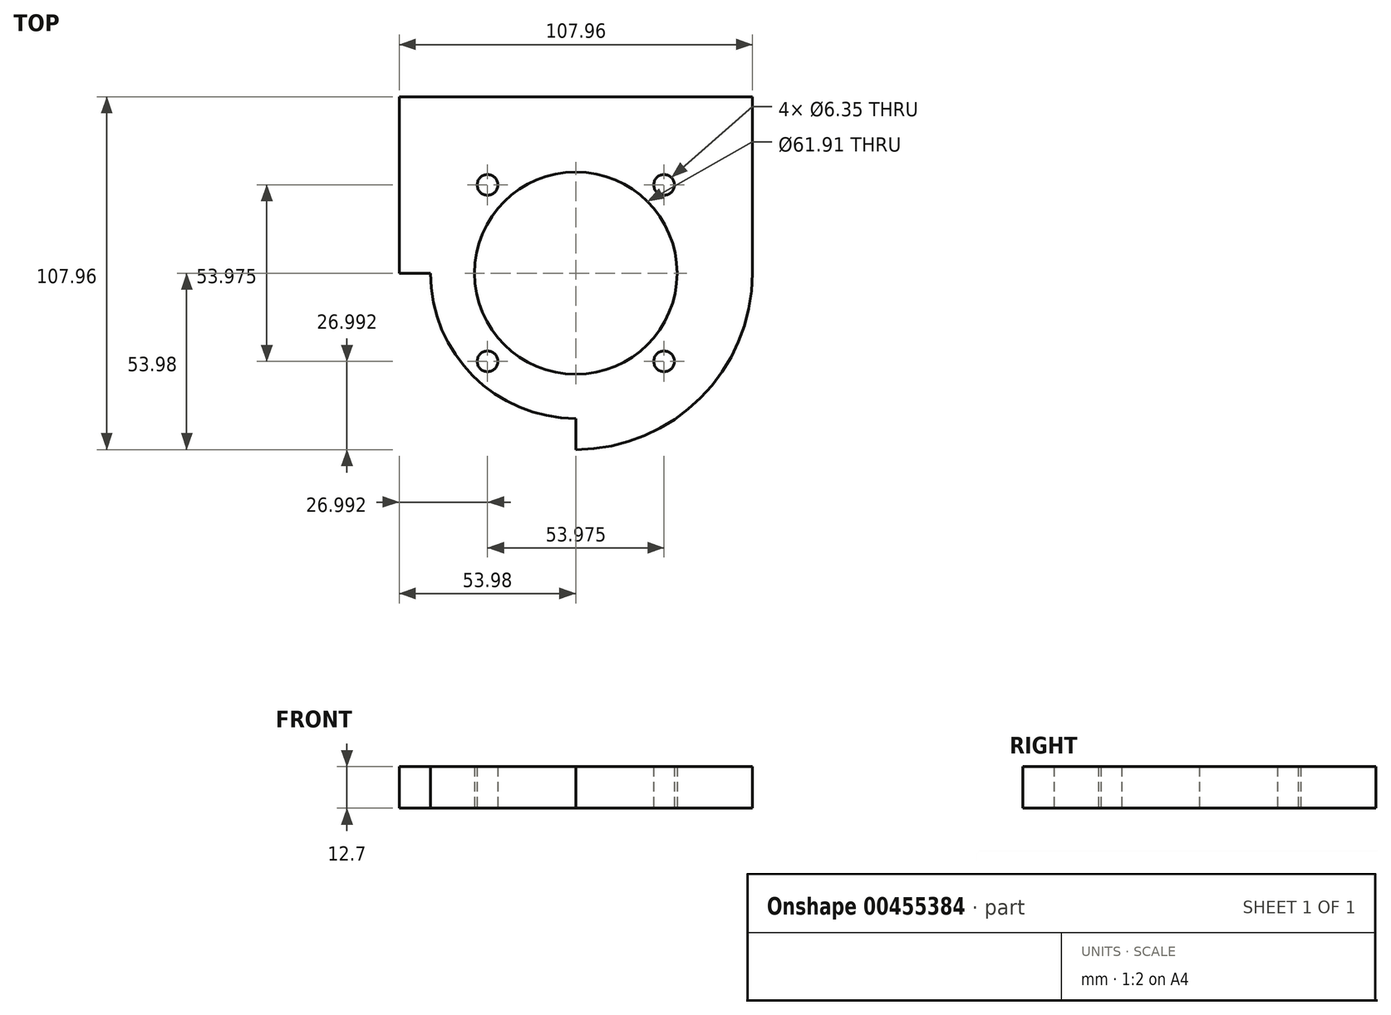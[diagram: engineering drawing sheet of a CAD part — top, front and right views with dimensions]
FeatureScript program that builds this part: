
annotation { "Feature Type Name" : "Feature", "Feature Type Description" : "" }
export const myFeature = defineFeature(function(context is Context, id is Id, definition is map)
    precondition{}
    {
        {
            var Q0;
            Q0=qCreatedBy(makeId("Top.planeOp"),FACE);
            var sketch = newSketch(context, id + "F0", { "sketchPlane" : qUnion([Q0])});
            skCircle(sketch, "E0", {"center": v(0, 0) * mm, "radius": 30.96 * mm});
            skArc(sketch, "E1", {"start": v(-44.45, 0) * mm, "mid": v(-31.43, -31.43) * mm, "end": v(0, -44.45) * mm});
            skArc(sketch, "E2", {"start": v(0, -53.98) * mm, "mid": v(38.17, -38.17) * mm, "end": v(53.98, 0) * mm});
            skLineSegment(sketch, "E3.top", {"start": v(53.97, 53.98) * mm, "end": v(-53.98, 53.97) * mm});
            skLineSegment(sketch, "E3.left", {"start": v(53.98, 0) * mm, "end": v(53.98, 53.98) * mm});
            skLineSegment(sketch, "E3.right", {"start": v(-53.98, 0) * mm, "end": v(-53.98, 53.97) * mm});
            skLineSegment(sketch, "E4", {"start": v(0, -44.45) * mm, "end": v(0, -53.98) * mm});
            skLineSegment(sketch, "E5.trimOffspring", {"start": v(-44.45, 0) * mm, "end": v(-53.97, 0) * mm});
            skLineSegment(sketch, "E6", {"start": v(0, 0) * mm, "end": v(53.97, 53.98) * mm, "construction": true});
            skCircle(sketch, "E7", {"center": v(0, 0) * mm, "radius": 44.45 * mm, "construction": true});
            skLineSegment(sketch, "E8", {"start": v(21.89, 21.89) * mm, "end": v(31.43, 31.43) * mm, "construction": true});
            skCircle(sketch, "E9", {"center": v(26.99, 26.99) * mm, "radius": 3.18 * mm});
            skCircle(sketch, "E10.1.0", {"center": v(-26.99, 26.99) * mm, "radius": 3.18 * mm});
            skCircle(sketch, "E10.2.0", {"center": v(-26.99, -26.99) * mm, "radius": 3.18 * mm});
            skCircle(sketch, "E10.3.0", {"center": v(26.99, -26.99) * mm, "radius": 3.18 * mm});
            skSolve(sketch);
        }
        {
            var Q0;
            Q0 = qSketchRegion(id + "F0", true);
            extrude(context, id + "F1", {"entities" : qUnion([Q0]), "depth" : 12.7 * mm});
        }
    });
